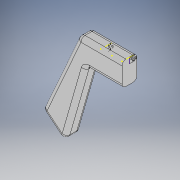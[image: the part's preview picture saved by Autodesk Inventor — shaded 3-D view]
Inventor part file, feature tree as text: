
AUTODESK INVENTOR PART (.ipt)
format: ipt  version: 2016 (Build 200138000, 138)  size: 187,904 bytes
history: native  units: mm
features: sketch x7, extrude x3, fillet x1
ambient origin geometry x8: Origin, YZ Plane, XZ Plane, XY Plane, X Axis, Y Axis, Z Axis, Center Point
bodies: Body1 (feature_tree), Body2 (feature_tree), Body3 (feature_tree)
feature tree (11):
  extrude  "Extrusion3"  Depth=24.0mm
  fillet  "Fillet3"  Radius=24.0mm
  sketch  "Sketch5"  dims[d44=28.8mm d45=4.0mm]
  extrude  "Extrusion4"  Depth=4.0mm
  sketch  "Sketch7"  dims[d49=5.9mm]
  extrude  "Extrusion5"  Depth=4.0mm
  sketch  "Sketch9"  dims[d54=10.0mm d55=0.0mm]
  sketch  "Sketch10"  dims[d56=5.9mm d57=5.9mm]
  sketch  "Sketch4"  dims[d40=22.5mm d41=90.0mm d43=24.0mm]
  sketch  "Sketch6"  dims[d46=15.0mm d47=0.0mm d48=4.0mm]
  sketch  "Sketch8"  dims[d50=11.5mm d51=0.0mm]
